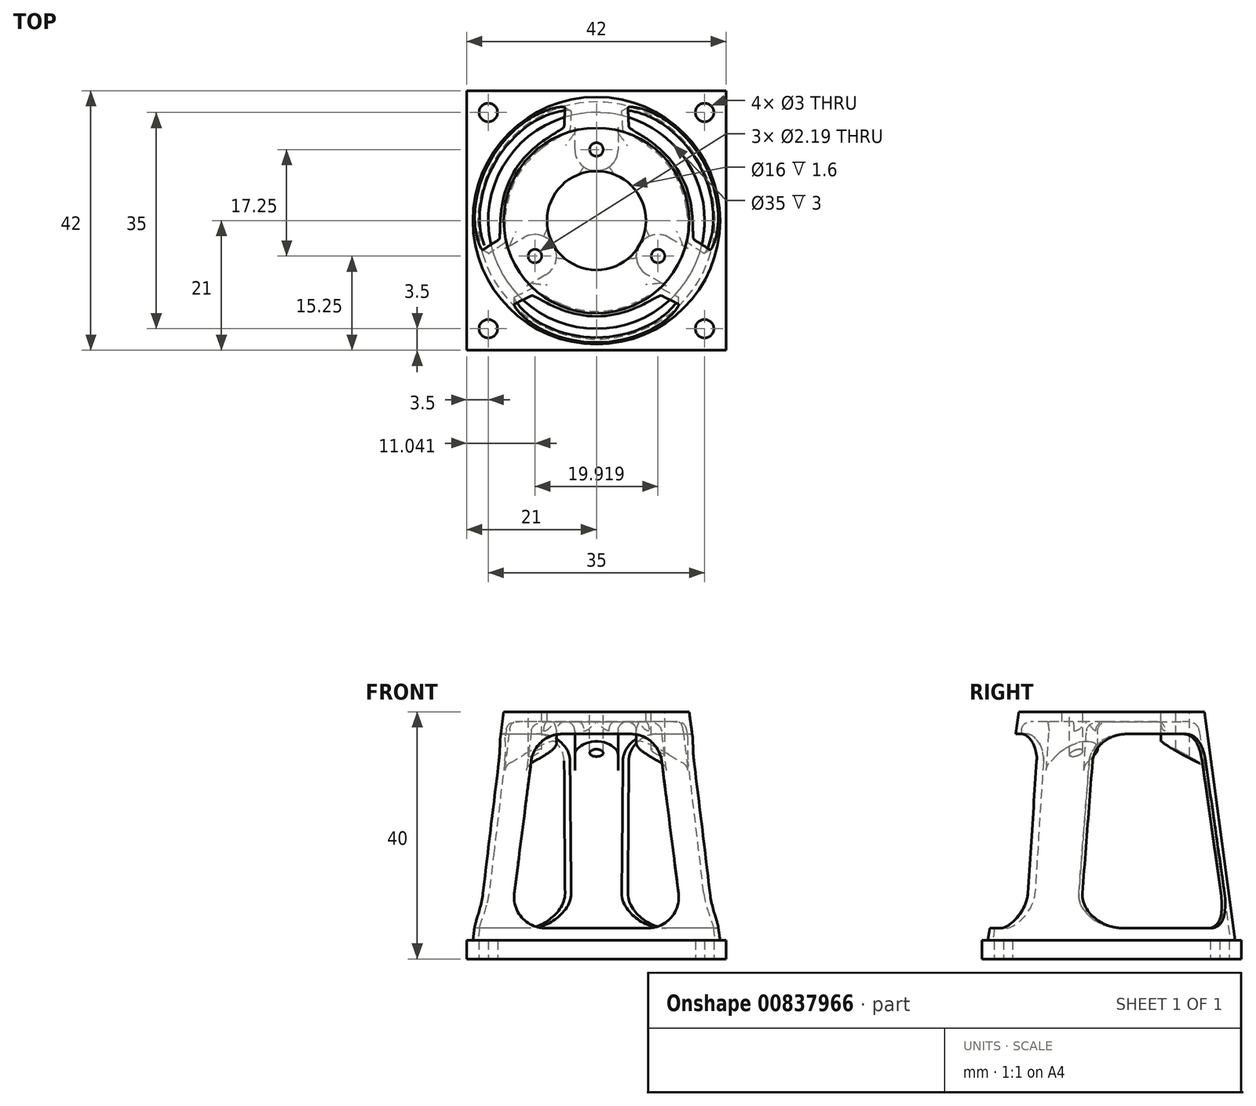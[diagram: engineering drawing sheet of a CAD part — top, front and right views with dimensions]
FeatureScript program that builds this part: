
annotation { "Feature Type Name" : "Feature", "Feature Type Description" : "" }
export const myFeature = defineFeature(function(context is Context, id is Id, definition is map)
    precondition{}
    {
        {
            var Q0;
            Q0=qCreatedBy(makeId("Top.planeOp"),FACE);
            var sketch = newSketch(context, id + "F0", { "sketchPlane" : qUnion([Q0])});
            skLineSegment(sketch, "E0.bottom", {"start": v(-17.5, 17.5) * mm, "end": v(17.5, 17.5) * mm, "construction": true});
            skLineSegment(sketch, "E0.top", {"start": v(-17.5, -17.5) * mm, "end": v(17.5, -17.5) * mm, "construction": true});
            skLineSegment(sketch, "E0.left", {"start": v(-17.5, 17.5) * mm, "end": v(-17.5, -17.5) * mm, "construction": true});
            skLineSegment(sketch, "E0.right", {"start": v(17.5, 17.5) * mm, "end": v(17.5, -17.5) * mm, "construction": true});
            skPoint(sketch, "E1", {"position": v(0, 17.5) * mm});
            skPoint(sketch, "E2", {"position": v(17.5, 0) * mm});
            skLineSegment(sketch, "E3.bottom", {"start": v(-21, 21) * mm, "end": v(21, 21) * mm});
            skLineSegment(sketch, "E3.top", {"start": v(-21, -21) * mm, "end": v(21, -21) * mm});
            skLineSegment(sketch, "E3.left", {"start": v(-21, 21) * mm, "end": v(-21, -21) * mm});
            skLineSegment(sketch, "E3.right", {"start": v(21, 21) * mm, "end": v(21, -21) * mm});
            skCircle(sketch, "E4", {"center": v(0, 0) * mm, "radius": 17.5 * mm});
            skCircle(sketch, "E5", {"center": v(-17.5, 17.5) * mm, "radius": 1.5 * mm});
            skCircle(sketch, "E6", {"center": v(17.5, 17.5) * mm, "radius": 1.5 * mm});
            skCircle(sketch, "E7", {"center": v(17.5, -17.5) * mm, "radius": 1.5 * mm});
            skCircle(sketch, "E8", {"center": v(-17.5, -17.5) * mm, "radius": 1.5 * mm});
            skPoint(sketch, "E9", {"position": v(21, 0) * mm});
            skPoint(sketch, "E10", {"position": v(0, 21) * mm});
            skSolve(sketch);
        }
        {
            var Q0;
            Q0 = qSketchRegion(id + "F0", true);
            extrude(context, id + "F1", {"entities" : qUnion([Q0]), "depth" : 3 * mm, "offsetDistance" : 25 * mm});
        }
        {
            var Q0;
            Q0=makeQuery(id+"F1.opExtrude","CAP_FACE",FACE,{"disambiguationData":[OSD([sQuery(id+"F0.wireOp",EDGE,"E3.bottom"),sQuery(id+"F0.wireOp",EDGE,"E3.top"),sQuery(id+"F0.wireOp",EDGE,"E3.left"),sQuery(id+"F0.wireOp",EDGE,"E3.right"),sQuery(id+"F0.wireOp",EDGE,"E4"),sQuery(id+"F0.wireOp",EDGE,"E5"),sQuery(id+"F0.wireOp",EDGE,"E6"),sQuery(id+"F0.wireOp",EDGE,"E7"),sQuery(id+"F0.wireOp",EDGE,"E8")])],"isStart":false});
            var sketch = newSketch(context, id + "F2", { "sketchPlane" : qUnion([Q0])});
            skCircle(sketch, "E11", {"center": v(0, 0) * mm, "radius": 20 * mm});
            skSolve(sketch);
        }
        {
            var Q0;
            Q0=qCreatedBy(makeId("Top.planeOp"),FACE);
            cPlane(context, id + "F3", {"entities" : qUnion([Q0]), "cplaneType" : CPlaneType.OFFSET, "offset" : 40 * mm, "width" : 150 * mm, "height" : 150 * mm});
        }
        {
            var Q0;
            Q0=qCreatedBy(id+"F3.planeOp",FACE);
            var sketch = newSketch(context, id + "F4", { "sketchPlane" : qUnion([Q0])});
            skCircle(sketch, "E12", {"center": v(0, 0) * mm, "radius": 15 * mm});
            skSolve(sketch);
        }
        {
            var Q0;
            Q0 = qSketchRegion(id + "F2", true);
            var Q1;
            Q1 = qSketchRegion(id + "F4", true);
            loft(context, id + "F5", {"sheetProfilesArray" : [{ "sheetProfileEntities" : qUnion([Q0]) }, { "sheetProfileEntities" : qUnion([Q1]) }]});
        }
        {
            var Q0;
            Q0=makeQuery(id+"F5.opLoft","CAP_FACE",FACE,{"disambiguationData":[OSD([makeQuery(id+"F2.imprint","IMPRINT",FACE,{"disambiguationData":[TD([[makeQuery(id+"F2.imprint","IMPRINT",EDGE,{"derivedFrom":makeQuery(id+"F1.opExtrude","CAP_EDGE",EDGE,{"disambiguationData":[OSD([sQuery(id+"F0.wireOp",EDGE,"E4")])],"isStart":false})}),-1.0]])]})])],"isStart":true});
            var Q1;
            Q1=makeQuery(id+"F5.opLoft","SWEPT_BODY",BODY,{"disambiguationData":[OSD([makeQuery(id+"F2.imprint","IMPRINT",FACE,{"disambiguationData":[TD([[makeQuery(id+"F2.imprint","IMPRINT",EDGE,{"derivedFrom":makeQuery(id+"F1.opExtrude","CAP_EDGE",EDGE,{"disambiguationData":[OSD([sQuery(id+"F0.wireOp",EDGE,"E4")])],"isStart":false})}),1.0]])]}),makeQuery(id+"F4.imprint","IMPRINT",FACE,{"disambiguationData":[TD([[makeQuery(id+"F4.imprint","IMPRINT",EDGE,{"derivedFrom":sQuery(id+"F4.wireOp",EDGE,"E12")}),1.0]])]})])]});
            shell(context, id + "F6", {"entities" : qUnion([Q0]), "parts" : qUnion([Q1]), "thickness" : 0.8 * mm});
        }
        {
            var Q0;
            Q0=qCreatedBy(id+"F3.planeOp",FACE);
            var sketch = newSketch(context, id + "F7", { "sketchPlane" : qUnion([Q0])});
            skCircle(sketch, "E13", {"center": v(0, 0) * mm, "radius": 15 * mm});
            skCircle(sketch, "E14", {"center": v(0, 0) * mm, "radius": 8 * mm});
            skSolve(sketch);
        }
        {
            var Q0;
            Q0=makeQuery(id+"F7.imprint","IMPRINT",FACE,{"disambiguationData":[TD([[makeQuery(id+"F7.imprint","IMPRINT",EDGE,{"derivedFrom":sQuery(id+"F7.wireOp",EDGE,"E13")}),1.0]])]});
            extrude(context, id + "F8", {"entities" : qUnion([Q0]), "operationType" : NewBodyOperationType.ADD, "oppositeDirection" : true, "depth" : (4 * 2 * 0.2) * mm, "offsetDistance" : 25 * mm});
        }
        {
            var Q0;
            Q0=makeQuery(id+"F7.imprint","IMPRINT",FACE,{"disambiguationData":[TD([[makeQuery(id+"F7.imprint","IMPRINT",EDGE,{"derivedFrom":sQuery(id+"F7.wireOp",EDGE,"E14")}),1.0]])]});
            extrude(context, id + "F9", {"entities" : qUnion([Q0]), "operationType" : NewBodyOperationType.REMOVE, "oppositeDirection" : true, "depth" : 25 * mm, "offsetDistance" : 25 * mm});
        }
        {
            var Q0;
            Q0=makeQuery(id+"F7.imprint","IMPRINT",FACE,{"disambiguationData":[TD([[makeQuery(id+"F7.imprint","IMPRINT",EDGE,{"derivedFrom":sQuery(id+"F7.wireOp",EDGE,"E13")}),1.0]])]});
            var sketch = newSketch(context, id + "F10", { "sketchPlane" : qUnion([Q0])});
            skLineSegment(sketch, "E15", {"start": v(0, 0) * mm, "end": v(0, 15) * mm, "construction": true});
            skCircle(sketch, "E16", {"center": v(0, 11.5) * mm, "radius": 1.5 * mm, "construction": true});
            skCircle(sketch, "E17", {"center": v(0, 11.5) * mm, "radius": 1.1 * mm});
            skCircle(sketch, "E18.1.0", {"center": v(-9.96, -5.75) * mm, "radius": 1.1 * mm});
            skCircle(sketch, "E18.2.0", {"center": v(9.96, -5.75) * mm, "radius": 1.1 * mm});
            skPoint(sketch, "E18.center", {"position": v(0, 0) * mm});
            skCircle(sketch, "E19", {"center": v(9.96, -5.75) * mm, "radius": 1.5 * mm, "construction": true});
            skLineSegment(sketch, "E20", {"start": v(0.75, 10.2) * mm, "end": v(9.2, -4.45) * mm, "construction": true});
            skArc(sketch, "E21", {"start": v(-3.5, 11.5) * mm, "mid": v(0, 8) * mm, "end": v(3.5, 11.5) * mm});
            skLineSegment(sketch, "E22", {"start": v(-3.5, 11.5) * mm, "end": v(3.5, 11.5) * mm, "construction": true});
            skLineSegment(sketch, "E23", {"start": v(-3.5, 11.5) * mm, "end": v(-3.5, 18.78) * mm});
            skLineSegment(sketch, "E24", {"start": v(-3.5, 18.78) * mm, "end": v(3.5, 18.78) * mm});
            skLineSegment(sketch, "E25", {"start": v(3.5, 18.78) * mm, "end": v(3.5, 11.5) * mm});
            skLineSegment(sketch, "E26.1.0", {"start": v(-18.01, -6.36) * mm, "end": v(-11.7, -2.72) * mm});
            skLineSegment(sketch, "E26.1.1", {"start": v(-14.51, -12.42) * mm, "end": v(-18.01, -6.36) * mm});
            skLineSegment(sketch, "E26.1.2", {"start": v(-8.2, -8.78) * mm, "end": v(-14.51, -12.42) * mm});
            skArc(sketch, "E26.1.3", {"start": v(-8.2, -8.78) * mm, "mid": v(-6.93, -4) * mm, "end": v(-11.7, -2.72) * mm});
            skLineSegment(sketch, "E26.2.0", {"start": v(14.51, -12.42) * mm, "end": v(8.2, -8.78) * mm});
            skLineSegment(sketch, "E26.2.1", {"start": v(18.01, -6.36) * mm, "end": v(14.51, -12.42) * mm});
            skLineSegment(sketch, "E26.2.2", {"start": v(11.7, -2.72) * mm, "end": v(18.01, -6.36) * mm});
            skArc(sketch, "E26.2.3", {"start": v(11.7, -2.72) * mm, "mid": v(6.93, -4) * mm, "end": v(8.2, -8.78) * mm});
            skSolve(sketch);
        }
        {
            var Q0;
            Q0=makeQuery(id+"F10.imprint","IMPRINT",FACE,{"disambiguationData":[TD([[makeQuery(id+"F10.imprint","IMPRINT",EDGE,{"derivedFrom":sQuery(id+"F10.wireOp",EDGE,"E17")}),-1.0]])]});
            var Q1;
            {var subQ0=sQuery(id+"F10.wireOp",EDGE,"E24");Q1=makeQuery(id+"F10.imprint","IMPRINT",FACE,{"disambiguationData":[TD([[makeQuery(id+"F10.imprint","IMPRINT",EDGE,{"derivedFrom":subQ0}),-1.0]])]});}
            var Q2;
            {var subQ0=sQuery(id+"F10.wireOp",EDGE,"E26.1.1");Q2=makeQuery(id+"F10.imprint","IMPRINT",FACE,{"disambiguationData":[TD([[makeQuery(id+"F10.imprint","IMPRINT",EDGE,{"derivedFrom":subQ0}),-1.0]])]});}
            var Q3;
            Q3=makeQuery(id+"F10.imprint","IMPRINT",FACE,{"disambiguationData":[TD([[makeQuery(id+"F10.imprint","IMPRINT",EDGE,{"derivedFrom":sQuery(id+"F10.wireOp",EDGE,"E18.1.0")}),-1.0]])]});
            var Q4;
            {var subQ0=sQuery(id+"F10.wireOp",EDGE,"E26.2.1");Q4=makeQuery(id+"F10.imprint","IMPRINT",FACE,{"disambiguationData":[TD([[makeQuery(id+"F10.imprint","IMPRINT",EDGE,{"derivedFrom":subQ0}),-1.0]])]});}
            var Q5;
            Q5=makeQuery(id+"F10.imprint","IMPRINT",FACE,{"disambiguationData":[TD([[makeQuery(id+"F10.imprint","IMPRINT",EDGE,{"derivedFrom":sQuery(id+"F10.wireOp",EDGE,"E18.2.0")}),-1.0]])]});
            extrude(context, id + "F11", {"entities" : qUnion([Q0, Q1, Q2, Q3, Q4, Q5]), "operationType" : NewBodyOperationType.ADD, "oppositeDirection" : true, "depth" : 9 * mm, "offsetDistance" : 25 * mm});
        }
        {
            var Q0;
            Q0=makeQuery(id+"F10.imprint","IMPRINT",FACE,{"disambiguationData":[TD([[makeQuery(id+"F10.imprint","IMPRINT",EDGE,{"derivedFrom":sQuery(id+"F10.wireOp",EDGE,"E17")}),1.0]])]});
            var Q1;
            Q1=makeQuery(id+"F10.imprint","IMPRINT",FACE,{"disambiguationData":[TD([[makeQuery(id+"F10.imprint","IMPRINT",EDGE,{"derivedFrom":sQuery(id+"F10.wireOp",EDGE,"E18.2.0")}),1.0]])]});
            var Q2;
            Q2=makeQuery(id+"F10.imprint","IMPRINT",FACE,{"disambiguationData":[TD([[makeQuery(id+"F10.imprint","IMPRINT",EDGE,{"derivedFrom":sQuery(id+"F10.wireOp",EDGE,"E18.1.0")}),1.0]])]});
            extrude(context, id + "F12", {"entities" : qUnion([Q0, Q1, Q2]), "operationType" : NewBodyOperationType.REMOVE, "oppositeDirection" : true, "depth" : 25 * mm, "offsetDistance" : 25 * mm});
        }
        {
            var Q0;
            Q0=qCreatedBy(makeId("Right.planeOp"),FACE);
            var sketch = newSketch(context, id + "F13", { "sketchPlane" : qUnion([Q0])});
            skLineSegment(sketch, "E27", {"start": v(0, 0) * mm, "end": v(0, 49.53) * mm, "construction": true});
            skLineSegment(sketch, "E28", {"start": v(15.37, 31.27) * mm, "end": v(19.2, 3) * mm});
            skLineSegment(sketch, "E29", {"start": v(19.2, 3) * mm, "end": v(0, 3) * mm});
            skLineSegment(sketch, "E30", {"start": v(15.37, 31.27) * mm, "end": v(7.3, 35.61) * mm});
            skLineSegment(sketch, "E31", {"start": v(7.3, 35.61) * mm, "end": v(0, 35.61) * mm});
            skLineSegment(sketch, "E32", {"start": v(0, 35.61) * mm, "end": v(0, 3) * mm});
            skLineSegment(sketch, "E33.0", {"start": v(-15, 40) * mm, "end": v(15, 40) * mm});
            skLineSegment(sketch, "E34", {"start": v(16.22, 31) * mm, "end": v(20, 3) * mm});
            skLineSegment(sketch, "E35", {"start": v(16.22, 31) * mm, "end": v(15, 40) * mm});
            skLineSegment(sketch, "E36", {"start": v(15, 40) * mm, "end": v(28.08, 40) * mm});
            skLineSegment(sketch, "E37", {"start": v(28.08, 40) * mm, "end": v(28.08, 3) * mm});
            skLineSegment(sketch, "E38", {"start": v(28.08, 3) * mm, "end": v(20, 3) * mm});
            skSolve(sketch);
        }
        {
            var Q0;
            Q0 = qSketchRegion(id + "F13", true);
            var Q1;
            Q1=sQuery(id+"F13.wireOp",EDGE,"E27");
            revolve(context, id + "F14", {"operationType" : NewBodyOperationType.REMOVE, "surfaceOperationType" : NewSurfaceOperationType.NEW, "entities" : qUnion([Q0]), "axis" : qUnion([Q1]), "revolveType" : RevolveType.FULL, "oppositeDirection" : true});
        }
        {
            var Q0;
            Q0=qCreatedBy(makeId("Front.planeOp"),FACE);
            cPlane(context, id + "F15", {"entities" : qUnion([Q0]), "cplaneType" : CPlaneType.OFFSET, "offset" : 25 * mm, "width" : 150 * mm, "height" : 150 * mm});
        }
        {
            var Q0;
            Q0=qCreatedBy(id+"F15.planeOp",FACE);
            var sketch = newSketch(context, id + "F16", { "sketchPlane" : qUnion([Q0])});
            skLineSegment(sketch, "E39", {"start": v(-10, 36.4) * mm, "end": v(10, 36.4) * mm});
            skLineSegment(sketch, "E40", {"start": v(10, 36.4) * mm, "end": v(14, 5) * mm});
            skLineSegment(sketch, "E41", {"start": v(14, 5) * mm, "end": v(-14, 5) * mm});
            skLineSegment(sketch, "E42", {"start": v(-14, 5) * mm, "end": v(-10, 36.4) * mm});
            skPoint(sketch, "E43", {"position": v(0, 36.4) * mm});
            skPoint(sketch, "E44", {"position": v(0, 5) * mm});
            skSolve(sketch);
        }
        {
            var Q0;
            Q0=makeQuery(id+"F16.imprint","IMPRINT",FACE,{"disambiguationData":[TD([[makeQuery(id+"F16.imprint","IMPRINT",EDGE,{"derivedFrom":sQuery(id+"F16.wireOp",EDGE,"E39")}),-1.0]])]});
            var Q1;
            Q1 = qConstructionFilter(qBodyType(qCreatedBy(id + "F16" ,EDGE), BodyType.WIRE), ConstructionObject.NO);
            extrude(context, id + "F17", {"entities" : qUnion([Q0]), "surfaceEntities" : qUnion([Q1]), "oppositeDirection" : true, "depth" : 14.5 * mm, "offsetDistance" : 25 * mm});
        }
        {
            var Q0;
            Q0=makeQuery(id+"F17.opExtrude","SWEPT_BODY",BODY,{"disambiguationData":[OSD([sQuery(id+"F16.wireOp",EDGE,"E39"),sQuery(id+"F16.wireOp",EDGE,"E40"),sQuery(id+"F16.wireOp",EDGE,"E41"),sQuery(id+"F16.wireOp",EDGE,"E42")])]});
            var Q1;
            Q1=sQuery(id+"F7.wireOp",EDGE,"E14");
            circularPattern(context, id + "F18", {"entities" : qUnion([Q0]), "axis" : qUnion([Q1]), "angle" : 360 * degree, "instanceCount" : 3, "equalSpace" : true});
        }
        {
            var Q0;
            Q0=makeQuery(id+"F17.opExtrude","SWEPT_BODY",BODY,{"disambiguationData":[OSD([sQuery(id+"F16.wireOp",EDGE,"E39"),sQuery(id+"F16.wireOp",EDGE,"E40"),sQuery(id+"F16.wireOp",EDGE,"E41"),sQuery(id+"F16.wireOp",EDGE,"E42")])]});
            var Q1;
            Q1=makeQuery(id+"F18.opPattern","COPY",BODY,{"derivedFrom":makeQuery(id+"F17.opExtrude","SWEPT_BODY",BODY,{"disambiguationData":[OSD([sQuery(id+"F16.wireOp",EDGE,"E39"),sQuery(id+"F16.wireOp",EDGE,"E40"),sQuery(id+"F16.wireOp",EDGE,"E41"),sQuery(id+"F16.wireOp",EDGE,"E42")])]}),"instanceName":"1"});
            var Q2;
            Q2=makeQuery(id+"F18.opPattern","COPY",BODY,{"derivedFrom":makeQuery(id+"F17.opExtrude","SWEPT_BODY",BODY,{"disambiguationData":[OSD([sQuery(id+"F16.wireOp",EDGE,"E39"),sQuery(id+"F16.wireOp",EDGE,"E40"),sQuery(id+"F16.wireOp",EDGE,"E41"),sQuery(id+"F16.wireOp",EDGE,"E42")])]}),"instanceName":"2"});
            var Q3;
            Q3=makeQuery(id+"F5.opLoft","SWEPT_BODY",BODY,{"disambiguationData":[OSD([makeQuery(id+"F2.imprint","IMPRINT",FACE,{"disambiguationData":[TD([[makeQuery(id+"F2.imprint","IMPRINT",EDGE,{"derivedFrom":makeQuery(id+"F1.opExtrude","CAP_EDGE",EDGE,{"disambiguationData":[OSD([sQuery(id+"F0.wireOp",EDGE,"E4")])],"isStart":false})}),1.0]])]}),makeQuery(id+"F4.imprint","IMPRINT",FACE,{"disambiguationData":[TD([[makeQuery(id+"F4.imprint","IMPRINT",EDGE,{"derivedFrom":sQuery(id+"F4.wireOp",EDGE,"E12")}),1.0]])]})])]});
            booleanBodies(context, id + "F19", {"operationType" : BooleanOperationType.SUBTRACTION, "tools" : qUnion([Q0, Q1, Q2]), "targets" : qUnion([Q3])});
        }
        {
            var Q0;
            {var subQ0=makeQuery(id+"F6.opShell","OFFSET_FACE",FACE,{"disambiguationData":[OSD([sQuery(id+"F2.wireOp",EDGE,"E11"),sQuery(id+"F4.wireOp",EDGE,"E12")])]});var subQ1=makeQuery(id+"F8.opExtrude","CAP_FACE",FACE,{"disambiguationData":[OSD([sQuery(id+"F7.wireOp",EDGE,"E13"),sQuery(id+"F7.wireOp",EDGE,"E14")])],"isStart":false});Q0=makeQuery(id+"F11.boolean.opBoolean","SPLIT",EDGE,{"disambiguationData":[TD([makeQuery(id+"F11.opExtrude","SWEPT_FACE",FACE,{"disambiguationData":[OSD([sQuery(id+"F10.wireOp",EDGE,"E26.1.2")])]})])],"derivedFrom":makeQuery(id+"F8.boolean.opBoolean","INTERSECT",EDGE,{"derivedFrom":[subQ0,subQ1]})});}
            var Q1;
            {var subQ0=makeQuery(id+"F6.opShell","OFFSET_FACE",FACE,{"disambiguationData":[OSD([sQuery(id+"F2.wireOp",EDGE,"E11"),sQuery(id+"F4.wireOp",EDGE,"E12")])]});var subQ1=makeQuery(id+"F8.opExtrude","CAP_FACE",FACE,{"disambiguationData":[OSD([sQuery(id+"F7.wireOp",EDGE,"E13"),sQuery(id+"F7.wireOp",EDGE,"E14")])],"isStart":false});Q1=makeQuery(id+"F11.boolean.opBoolean","SPLIT",EDGE,{"disambiguationData":[TD([makeQuery(id+"F11.opExtrude","SWEPT_FACE",FACE,{"disambiguationData":[OSD([sQuery(id+"F10.wireOp",EDGE,"E25")])]})])],"derivedFrom":makeQuery(id+"F8.boolean.opBoolean","INTERSECT",EDGE,{"derivedFrom":[subQ0,subQ1]})});}
            var Q2;
            {var subQ0=makeQuery(id+"F6.opShell","OFFSET_FACE",FACE,{"disambiguationData":[OSD([sQuery(id+"F2.wireOp",EDGE,"E11"),sQuery(id+"F4.wireOp",EDGE,"E12")])]});var subQ1=makeQuery(id+"F8.opExtrude","CAP_FACE",FACE,{"disambiguationData":[OSD([sQuery(id+"F7.wireOp",EDGE,"E13"),sQuery(id+"F7.wireOp",EDGE,"E14")])],"isStart":false});Q2=makeQuery(id+"F11.boolean.opBoolean","SPLIT",EDGE,{"disambiguationData":[TD([makeQuery(id+"F11.opExtrude","SWEPT_FACE",FACE,{"disambiguationData":[OSD([sQuery(id+"F10.wireOp",EDGE,"E23")])]})])],"derivedFrom":makeQuery(id+"F8.boolean.opBoolean","INTERSECT",EDGE,{"derivedFrom":[subQ0,subQ1]})});}
            var Q3;
            Q3=makeQuery(id+"F11.boolean.opBoolean","INTERSECT",EDGE,{"disambiguationData":[OD(1.0)],"derivedFrom":[makeQuery(id+"F8.opExtrude","CAP_FACE",FACE,{"disambiguationData":[OSD([sQuery(id+"F7.wireOp",EDGE,"E13"),sQuery(id+"F7.wireOp",EDGE,"E14")])],"isStart":false}),makeQuery(id+"F11.opExtrude","SWEPT_FACE",FACE,{"disambiguationData":[OSD([sQuery(id+"F10.wireOp",EDGE,"E26.1.3")])]})]});
            var Q4;
            Q4=makeQuery(id+"F11.boolean.opBoolean","INTERSECT",EDGE,{"disambiguationData":[OD(0.0)],"derivedFrom":[makeQuery(id+"F8.opExtrude","CAP_FACE",FACE,{"disambiguationData":[OSD([sQuery(id+"F7.wireOp",EDGE,"E13"),sQuery(id+"F7.wireOp",EDGE,"E14")])],"isStart":false}),makeQuery(id+"F11.opExtrude","SWEPT_FACE",FACE,{"disambiguationData":[OSD([sQuery(id+"F10.wireOp",EDGE,"E26.2.3")])]})]});
            var Q5;
            Q5=makeQuery(id+"F11.boolean.opBoolean","INTERSECT",EDGE,{"disambiguationData":[OD(0.0)],"derivedFrom":[makeQuery(id+"F8.opExtrude","CAP_FACE",FACE,{"disambiguationData":[OSD([sQuery(id+"F7.wireOp",EDGE,"E13"),sQuery(id+"F7.wireOp",EDGE,"E14")])],"isStart":false}),makeQuery(id+"F11.opExtrude","SWEPT_FACE",FACE,{"disambiguationData":[OSD([sQuery(id+"F10.wireOp",EDGE,"E21")])]})]});
            var Q6;
            {var subQ0=sQuery(id+"F13.wireOp",EDGE,"E28");var subQ1=sQuery(id+"F13.wireOp",EDGE,"E30");Q6=makeQuery(id+"F14.boolean.opBoolean","COPY",EDGE,{"disambiguationData":[TD([makeQuery(id+"F11.opExtrude","SWEPT_FACE",FACE,{"disambiguationData":[OSD([sQuery(id+"F10.wireOp",EDGE,"E26.2.0")])]})])],"derivedFrom":makeQuery(id+"F14.opRevolve","SWEPT_EDGE",EDGE,{"disambiguationData":[OSD([subQ0,subQ1])]})});}
            var Q7;
            {var subQ0=sQuery(id+"F13.wireOp",EDGE,"E28");var subQ1=sQuery(id+"F13.wireOp",EDGE,"E30");Q7=makeQuery(id+"F14.boolean.opBoolean","COPY",EDGE,{"disambiguationData":[TD([makeQuery(id+"F11.opExtrude","SWEPT_FACE",FACE,{"disambiguationData":[OSD([sQuery(id+"F10.wireOp",EDGE,"E23")])]})])],"derivedFrom":makeQuery(id+"F14.opRevolve","SWEPT_EDGE",EDGE,{"disambiguationData":[OSD([subQ0,subQ1])]})});}
            var Q8;
            {var subQ0=sQuery(id+"F13.wireOp",EDGE,"E30");var subQ1=sQuery(id+"F13.wireOp",EDGE,"E28");Q8=makeQuery(id+"F14.boolean.opBoolean","COPY",EDGE,{"disambiguationData":[TD([makeQuery(id+"F11.opExtrude","SWEPT_FACE",FACE,{"disambiguationData":[OSD([sQuery(id+"F10.wireOp",EDGE,"E26.1.0")])]})])],"derivedFrom":makeQuery(id+"F14.opRevolve","SWEPT_EDGE",EDGE,{"disambiguationData":[OSD([subQ1,subQ0])]})});}
            fillet(context, id + "F20", {"entities" : qUnion([Q0, Q1, Q2, Q3, Q4, Q5, Q6, Q7, Q8]), "radius" : 1.5 * mm, "tangentPropagation" : true, "allowEdgeOverflow" : false});
        }
        {
            var Q0;
            Q0=makeQuery(id+"F19.opBoolean","COPY",EDGE,{"derivedFrom":makeQuery(id+"F18.opPattern","COPY",EDGE,{"derivedFrom":makeQuery(id+"F17.opExtrude","SWEPT_EDGE",EDGE,{"disambiguationData":[OSD([sQuery(id+"F16.wireOp",EDGE,"E41"),sQuery(id+"F16.wireOp",EDGE,"E42")])]}),"instanceName":"2"})});
            var Q1;
            Q1=makeQuery(id+"F19.opBoolean","COPY",EDGE,{"derivedFrom":makeQuery(id+"F18.opPattern","COPY",EDGE,{"derivedFrom":makeQuery(id+"F17.opExtrude","SWEPT_EDGE",EDGE,{"disambiguationData":[OSD([sQuery(id+"F16.wireOp",EDGE,"E40"),sQuery(id+"F16.wireOp",EDGE,"E41")])]}),"instanceName":"2"})});
            var Q2;
            Q2=makeQuery(id+"F19.opBoolean","COPY",EDGE,{"derivedFrom":makeQuery(id+"F17.opExtrude","SWEPT_EDGE",EDGE,{"disambiguationData":[OSD([sQuery(id+"F16.wireOp",EDGE,"E41"),sQuery(id+"F16.wireOp",EDGE,"E42")])]})});
            var Q3;
            Q3=makeQuery(id+"F19.opBoolean","COPY",EDGE,{"derivedFrom":makeQuery(id+"F17.opExtrude","SWEPT_EDGE",EDGE,{"disambiguationData":[OSD([sQuery(id+"F16.wireOp",EDGE,"E40"),sQuery(id+"F16.wireOp",EDGE,"E41")])]})});
            var Q4;
            Q4=makeQuery(id+"F19.opBoolean","COPY",EDGE,{"derivedFrom":makeQuery(id+"F18.opPattern","COPY",EDGE,{"derivedFrom":makeQuery(id+"F17.opExtrude","SWEPT_EDGE",EDGE,{"disambiguationData":[OSD([sQuery(id+"F16.wireOp",EDGE,"E41"),sQuery(id+"F16.wireOp",EDGE,"E42")])]}),"instanceName":"1"})});
            var Q5;
            Q5=makeQuery(id+"F19.opBoolean","COPY",EDGE,{"derivedFrom":makeQuery(id+"F18.opPattern","COPY",EDGE,{"derivedFrom":makeQuery(id+"F17.opExtrude","SWEPT_EDGE",EDGE,{"disambiguationData":[OSD([sQuery(id+"F16.wireOp",EDGE,"E40"),sQuery(id+"F16.wireOp",EDGE,"E41")])]}),"instanceName":"1"})});
            var Q6;
            Q6=makeQuery(id+"F19.opBoolean","COPY",EDGE,{"derivedFrom":makeQuery(id+"F18.opPattern","COPY",EDGE,{"derivedFrom":makeQuery(id+"F17.opExtrude","SWEPT_EDGE",EDGE,{"disambiguationData":[OSD([sQuery(id+"F16.wireOp",EDGE,"E39"),sQuery(id+"F16.wireOp",EDGE,"E40")])]}),"instanceName":"1"})});
            var Q7;
            Q7=makeQuery(id+"F19.opBoolean","COPY",EDGE,{"derivedFrom":makeQuery(id+"F18.opPattern","COPY",EDGE,{"derivedFrom":makeQuery(id+"F17.opExtrude","SWEPT_EDGE",EDGE,{"disambiguationData":[OSD([sQuery(id+"F16.wireOp",EDGE,"E39"),sQuery(id+"F16.wireOp",EDGE,"E42")])]}),"instanceName":"1"})});
            var Q8;
            Q8=makeQuery(id+"F19.opBoolean","COPY",EDGE,{"derivedFrom":makeQuery(id+"F17.opExtrude","SWEPT_EDGE",EDGE,{"disambiguationData":[OSD([sQuery(id+"F16.wireOp",EDGE,"E39"),sQuery(id+"F16.wireOp",EDGE,"E40")])]})});
            var Q9;
            Q9=makeQuery(id+"F19.opBoolean","COPY",EDGE,{"derivedFrom":makeQuery(id+"F17.opExtrude","SWEPT_EDGE",EDGE,{"disambiguationData":[OSD([sQuery(id+"F16.wireOp",EDGE,"E39"),sQuery(id+"F16.wireOp",EDGE,"E42")])]})});
            var Q10;
            Q10=makeQuery(id+"F19.opBoolean","COPY",EDGE,{"derivedFrom":makeQuery(id+"F18.opPattern","COPY",EDGE,{"derivedFrom":makeQuery(id+"F17.opExtrude","SWEPT_EDGE",EDGE,{"disambiguationData":[OSD([sQuery(id+"F16.wireOp",EDGE,"E39"),sQuery(id+"F16.wireOp",EDGE,"E40")])]}),"instanceName":"2"})});
            var Q11;
            Q11=makeQuery(id+"F19.opBoolean","COPY",EDGE,{"derivedFrom":makeQuery(id+"F18.opPattern","COPY",EDGE,{"derivedFrom":makeQuery(id+"F17.opExtrude","SWEPT_EDGE",EDGE,{"disambiguationData":[OSD([sQuery(id+"F16.wireOp",EDGE,"E39"),sQuery(id+"F16.wireOp",EDGE,"E42")])]}),"instanceName":"2"})});
            fillet(context, id + "F21", {"entities" : qUnion([Q0, Q1, Q2, Q3, Q4, Q5, Q6, Q7, Q8, Q9, Q10, Q11]), "radius" : 5 * mm, "allowEdgeOverflow" : false});
        }
    });
